# Revit family: 54-3334-001 DN350-600
name_source: partatom
category: Pipe Accessories
units: mm (PartAtom-declared; Revit-internal decimal feet)

## family parameters
Always vertical = No
Cut with Voids When Loaded = No
Part Type = Valve - Breaks Into
Round Connector Dimension = Use Diameter
Shared = No
Work Plane-Based = No

## types (25) — shared parameters
1 = 1 mm  [stored 0.00328084 ft]
50 = 40 mm
54-0350-33-0101100 = DN350_ PN10_ CTC
54-0350-33-1101100 = DN350_ PN16_ CTC
54-0350-34-0101100 = DN350_ PN10_ CTO
54-0350-34-1101100 = DN350_ PN16_ CTO
54-0400-33-0101100 = DN400_ PN10_ CTC
54-0400-33-1101100 = DN400_ PN16_ CTC
54-0400-33-1102100 = DN400_ PN16_ CTC
54-0400-34-0101100 = DN400_ PN10_ CTO
54-0400-34-1101100 = DN400_PN16_ CTO
54-0450-33-0101100 = DN450_ PN10_ CTC
54-0450-33-1101100 = DN450_ PN16_ CTC
54-0450-33-1102100 = DN450_ PN16_ CTC
54-0450-34-0101100 = DN450_ PN10_ CTO
54-0450-34-1101100 = DN450_ PN16_ CTO
54-0500-33-0101100 = DN500_ PN10_ CTC
54-0500-33-0102100 = DN500_ PN10_ CTC
54-0500-33-1101100 = DN500_ PN16_ CTC
54-0500-33-1102100 = DN500_ PN16_ CTC
54-0500-34-0101100 = DN500_ PN10_ CTO
54-0500-34-1101100 = DN500_ PN16_ CTO
54-0600-33-0101100 = DN600_ PN10_ CTC
54-0600-33-1101100 = DN600_ PN16_ CTC
54-0600-33-1102100 = DN600_ PN16_ CTC
54-0600-34-0101100 = DN600_ PN10_ CTO
54-0600-34-1101100 = DN600_ PN16_ CTO
Description_ = AVK GATE VALVE, FLANGED, METAL SEATED, PN10/16
F = 40 mm
F1 = 48 mm
F2 = 162 mm
H = 782 mm
Search_table = 54-3334-001 DN350-600
Stem_dim = 81 mm
URL product pages = https://www.avkvalves.com
stem_dim = 67.2 mm
sweep = 4 mm  [stored 0.0131234 ft]
zero-valued in all types: Default Elevation

## per-type parameters (varying)
- 54-0350-33-0101100: ACtuator_T=17.64 mm  [stored 0.057874 ft]; ADN=350 mm; Actuator_FLR=87.5 mm; BP_centre=50.5 mm; Body_H=391 mm; Body_L=448 mm; Body_T=167.5 mm; Body_W=198 mm; Body_rib_T=9.8 mm  [stored 0.0321522 ft]; Bonnet_FL_L=560 mm; Bonnet_FL_T=46.55 mm; Bonnet_FL_W=264 mm; Bonnet_dim1=89.6 mm; Bonnet_dim2=69.3 mm; Bonnet_dim3=649.06 mm; Bonnet_fillet=22 mm  [stored 0.0721785 ft]; Bore=175 mm; By_Vale_StemH1=168.75 mm; By_Vale_StemH2=177.19 mm; By_Vale_StemR1=14.67 mm; By_Vale_StemR2=26.4 mm; Bypass_DN=50 mm; Bypass_dim1=101 mm; Bypass_dim2=10.1 mm  [stored 0.0331365 ft]; Bypass_dim3=43.43 mm; Bypass_dis=430.95 mm; Bypass_dis/2=215.48 mm; Bypass_valve_H1=90 mm; Bypass_valve_H2=60 mm; Bypass_valve_H3=225 mm; Bypass_valve_W1=476.58 mm; Bypass_valve_W2=66 mm; Cut_dis=23.28 mm; DN=350 mm; FL_T=24.5 mm  [stored 0.0803806 ft]; Fillet=66 mm; H1=782 mm; H2=265 mm; L=381 mm; OD=505 mm; PN=10 mm  [stored 0.0328084 ft]; Raised_dia=429 mm; Raised_dis=4 mm  [stored 0.0131234 ft]; Rib_H=312.8 mm; Rib_L=252 mm; Rib_W=118.8 mm; W=787 mm; W-W1=280 mm; W1=507 mm; W1/2=253.5 mm; W_half=280 mm; bottom_rib=252.5 mm; bypass_sweep_dis=405.6 mm; wedge_dim1=217.8 mm
- 54-0350-33-1101100: ACtuator_T=19.08 mm  [stored 0.0625984 ft]; ADN=350 mm; Actuator_FLR=87.5 mm; BP_centre=53 mm; Body_H=391 mm; Body_L=448 mm; Body_T=167.5 mm; Body_W=198 mm; Body_rib_T=10.6 mm  [stored 0.0347769 ft]; Bonnet_FL_L=560 mm; Bonnet_FL_T=50.35 mm; Bonnet_FL_W=264 mm; Bonnet_dim1=89.6 mm; Bonnet_dim2=69.3 mm; Bonnet_dim3=649.06 mm; Bonnet_fillet=22 mm  [stored 0.0721785 ft]; Bore=175.05 mm; By_Vale_StemH1=168.75 mm; By_Vale_StemH2=177.19 mm; By_Vale_StemR1=14.67 mm; By_Vale_StemR2=26.4 mm; Bypass_DN=50 mm; Bypass_dim1=106 mm; Bypass_dim2=10.6 mm  [stored 0.0347769 ft]; Bypass_dim3=45.58 mm; Bypass_dis=430.95 mm; Bypass_dis/2=215.48 mm; Bypass_valve_H1=90 mm; Bypass_valve_H2=60 mm; Bypass_valve_H3=225 mm; Bypass_valve_W1=476.58 mm; Bypass_valve_W2=66 mm; Cut_dis=25.18 mm; DN=350.1 mm; FL_T=26.5 mm; Fillet=66 mm; H1=782 mm; H2=265 mm; L=381 mm; OD=530 mm; PN=16 mm  [stored 0.0524934 ft]; Raised_dia=429 mm; Raised_dis=4 mm  [stored 0.0131234 ft]; Rib_H=312.8 mm; Rib_L=252 mm; Rib_W=118.8 mm; W=787 mm; W-W1=280 mm; W1=507 mm; W1/2=253.5 mm; W_half=280 mm; bottom_rib=265 mm; bypass_sweep_dis=405.6 mm; wedge_dim1=217.8 mm
- 54-0350-34-0101100: ACtuator_T=17.64 mm  [stored 0.057874 ft]; ADN=350 mm; Actuator_FLR=87.5 mm; BP_centre=50.5 mm; Body_H=391 mm; Body_L=448 mm; Body_T=167.5 mm; Body_W=198 mm; Body_rib_T=9.8 mm  [stored 0.0321522 ft]; Bonnet_FL_L=560 mm; Bonnet_FL_T=46.55 mm; Bonnet_FL_W=264 mm; Bonnet_dim1=89.6 mm; Bonnet_dim2=69.3 mm; Bonnet_dim3=649.06 mm; Bonnet_fillet=22 mm  [stored 0.0721785 ft]; Bore=175.06 mm; By_Vale_StemH1=168.75 mm; By_Vale_StemH2=177.19 mm; By_Vale_StemR1=14.67 mm; By_Vale_StemR2=26.4 mm; Bypass_DN=50 mm; Bypass_dim1=101 mm; Bypass_dim2=10.1 mm  [stored 0.0331365 ft]; Bypass_dim3=43.43 mm; Bypass_dis=430.95 mm; Bypass_dis/2=215.48 mm; Bypass_valve_H1=90 mm; Bypass_valve_H2=60 mm; Bypass_valve_H3=225 mm; Bypass_valve_W1=476.58 mm; Bypass_valve_W2=66 mm; Cut_dis=23.28 mm; DN=350.11 mm; FL_T=24.5 mm  [stored 0.0803806 ft]; Fillet=66 mm; H1=782 mm; H2=265 mm; L=381 mm; OD=505 mm; PN=10 mm  [stored 0.0328084 ft]; Raised_dia=429 mm; Raised_dis=4 mm  [stored 0.0131234 ft]; Rib_H=312.8 mm; Rib_L=252 mm; Rib_W=118.8 mm; W=787 mm; W-W1=280 mm; W1=507 mm; W1/2=253.5 mm; W_half=280 mm; bottom_rib=252.5 mm; bypass_sweep_dis=405.6 mm; wedge_dim1=217.8 mm
- 54-0350-34-1101100: ACtuator_T=19.08 mm  [stored 0.0625984 ft]; ADN=350 mm; Actuator_FLR=87.5 mm; BP_centre=53 mm; Body_H=391 mm; Body_L=448 mm; Body_T=167.5 mm; Body_W=198 mm; Body_rib_T=10.6 mm  [stored 0.0347769 ft]; Bonnet_FL_L=560 mm; Bonnet_FL_T=50.35 mm; Bonnet_FL_W=264 mm; Bonnet_dim1=89.6 mm; Bonnet_dim2=69.3 mm; Bonnet_dim3=649.06 mm; Bonnet_fillet=22 mm  [stored 0.0721785 ft]; Bore=175.06 mm; By_Vale_StemH1=168.75 mm; By_Vale_StemH2=177.19 mm; By_Vale_StemR1=14.67 mm; By_Vale_StemR2=26.4 mm; Bypass_DN=50 mm; Bypass_dim1=106 mm; Bypass_dim2=10.6 mm  [stored 0.0347769 ft]; Bypass_dim3=45.58 mm; Bypass_dis=430.95 mm; Bypass_dis/2=215.48 mm; Bypass_valve_H1=90 mm; Bypass_valve_H2=60 mm; Bypass_valve_H3=225 mm; Bypass_valve_W1=476.58 mm; Bypass_valve_W2=66 mm; Cut_dis=25.18 mm; DN=350.12 mm; FL_T=26.5 mm; Fillet=66 mm; H1=782 mm; H2=265 mm; L=381 mm; OD=530 mm; PN=16 mm  [stored 0.0524934 ft]; Raised_dia=429 mm; Raised_dis=4 mm  [stored 0.0131234 ft]; Rib_H=312.8 mm; Rib_L=252 mm; Rib_W=118.8 mm; W=787 mm; W-W1=280 mm; W1=507 mm; W1/2=253.5 mm; W_half=280 mm; bottom_rib=265 mm; bypass_sweep_dis=405.6 mm; wedge_dim1=217.8 mm
- 54-0400-33-0101100: ACtuator_T=17.64 mm  [stored 0.057874 ft]; ADN=400 mm; Actuator_FLR=87.5 mm; BP_centre=56.5 mm; Body_H=428.5 mm; Body_L=483.2 mm; Body_T=192.5 mm; Body_W=198 mm; Body_rib_T=9.8 mm  [stored 0.0321522 ft]; Bonnet_FL_L=604 mm; Bonnet_FL_T=46.55 mm; Bonnet_FL_W=264 mm; Bonnet_dim1=96.64 mm; Bonnet_dim2=69.3 mm; Bonnet_dim3=711.31 mm; Bonnet_fillet=22 mm  [stored 0.0721785 ft]; Bore=200 mm; By_Vale_StemH1=168.75 mm; By_Vale_StemH2=177.19 mm; By_Vale_StemR1=14.67 mm; By_Vale_StemR2=26.4 mm; Bypass_DN=50 mm; Bypass_dim1=113 mm; Bypass_dim2=11.3 mm  [stored 0.0370735 ft]; Bypass_dim3=48.59 mm; Bypass_dis=456.45 mm; Bypass_dis/2=228.23 mm; Bypass_valve_H1=90 mm; Bypass_valve_H2=60 mm; Bypass_valve_H3=225 mm; Bypass_valve_W1=504.78 mm; Bypass_valve_W2=66 mm; Cut_dis=23.28 mm; DN=400 mm; FL_T=24.5 mm  [stored 0.0803806 ft]; Fillet=66 mm; H1=857 mm; H2=295 mm; L=406 mm; OD=565 mm; PN=10 mm  [stored 0.0328084 ft]; Raised_dia=480 mm; Raised_dis=4 mm  [stored 0.0131234 ft]; Rib_H=342.8 mm; Rib_L=271.8 mm; Rib_W=118.8 mm; W=839 mm; W-W1=302 mm; W1=537 mm; W1/2=268.5 mm; W_half=302 mm; bottom_rib=282.5 mm; bypass_sweep_dis=429.6 mm; wedge_dim1=217.8 mm
- 54-0400-33-1101100: ACtuator_T=20.16 mm  [stored 0.0661417 ft]; ADN=400 mm; Actuator_FLR=87.5 mm; BP_centre=59 mm; Body_H=428.5 mm; Body_L=483.2 mm; Body_T=192.5 mm; Body_W=198 mm; Body_rib_T=11.2 mm  [stored 0.0367454 ft]; Bonnet_FL_L=604 mm; Bonnet_FL_T=53.2 mm; Bonnet_FL_W=264 mm; Bonnet_dim1=96.64 mm; Bonnet_dim2=69.3 mm; Bonnet_dim3=711.31 mm; Bonnet_fillet=22 mm  [stored 0.0721785 ft]; Bore=200.05 mm; By_Vale_StemH1=168.75 mm; By_Vale_StemH2=177.19 mm; By_Vale_StemR1=14.67 mm; By_Vale_StemR2=26.4 mm; Bypass_DN=50 mm; Bypass_dim1=118 mm; Bypass_dim2=11.8 mm  [stored 0.0387139 ft]; Bypass_dim3=50.74 mm; Bypass_dis=456.45 mm; Bypass_dis/2=228.23 mm; Bypass_valve_H1=90 mm; Bypass_valve_H2=60 mm; Bypass_valve_H3=225 mm; Bypass_valve_W1=504.78 mm; Bypass_valve_W2=66 mm; Cut_dis=26.6 mm; DN=400.1 mm; FL_T=28 mm; Fillet=66 mm; H1=857 mm; H2=295 mm; L=406 mm; OD=590 mm; PN=16 mm  [stored 0.0524934 ft]; Raised_dia=480 mm; Raised_dis=4 mm  [stored 0.0131234 ft]; Rib_H=342.8 mm; Rib_L=271.8 mm; Rib_W=118.8 mm; W=839 mm; W-W1=302 mm; W1=537 mm; W1/2=268.5 mm; W_half=302 mm; bottom_rib=295 mm; bypass_sweep_dis=429.6 mm; wedge_dim1=217.8 mm
- 54-0400-33-1102100: ACtuator_T=20.16 mm  [stored 0.0661417 ft]; ADN=400 mm; Actuator_FLR=105 mm; BP_centre=59 mm; Body_H=428.5 mm; Body_L=483.2 mm; Body_T=192.5 mm; Body_W=198 mm; Body_rib_T=11.2 mm  [stored 0.0367454 ft]; Bonnet_FL_L=604 mm; Bonnet_FL_T=53.2 mm; Bonnet_FL_W=264 mm; Bonnet_dim1=96.64 mm; Bonnet_dim2=69.3 mm; Bonnet_dim3=711.31 mm; Bonnet_fillet=22 mm  [stored 0.0721785 ft]; Bore=200.06 mm; By_Vale_StemH1=168.75 mm; By_Vale_StemH2=177.19 mm; By_Vale_StemR1=14.67 mm; By_Vale_StemR2=26.4 mm; Bypass_DN=50 mm; Bypass_dim1=118 mm; Bypass_dim2=11.8 mm  [stored 0.0387139 ft]; Bypass_dim3=50.74 mm; Bypass_dis=456.45 mm; Bypass_dis/2=228.23 mm; Bypass_valve_H1=90 mm; Bypass_valve_H2=60 mm; Bypass_valve_H3=225 mm; Bypass_valve_W1=504.78 mm; Bypass_valve_W2=66 mm; Cut_dis=26.6 mm; DN=400.11 mm; FL_T=28 mm; Fillet=66 mm; H1=857 mm; H2=295 mm; L=406 mm; OD=590 mm; PN=16 mm  [stored 0.0524934 ft]; Raised_dia=480 mm; Raised_dis=4 mm  [stored 0.0131234 ft]; Rib_H=342.8 mm; Rib_L=271.8 mm; Rib_W=118.8 mm; W=839 mm; W-W1=302 mm; W1=537 mm; W1/2=268.5 mm; W_half=302 mm; bottom_rib=295 mm; bypass_sweep_dis=429.6 mm; wedge_dim1=217.8 mm
- 54-0400-34-0101100: ACtuator_T=17.64 mm  [stored 0.057874 ft]; ADN=400 mm; Actuator_FLR=87.5 mm; BP_centre=56.5 mm; Body_H=428.5 mm; Body_L=483.2 mm; Body_T=192.5 mm; Body_W=198 mm; Body_rib_T=9.8 mm  [stored 0.0321522 ft]; Bonnet_FL_L=604 mm; Bonnet_FL_T=46.55 mm; Bonnet_FL_W=264 mm; Bonnet_dim1=96.64 mm; Bonnet_dim2=69.3 mm; Bonnet_dim3=711.31 mm; Bonnet_fillet=22 mm  [stored 0.0721785 ft]; Bore=200.06 mm; By_Vale_StemH1=168.75 mm; By_Vale_StemH2=177.19 mm; By_Vale_StemR1=14.67 mm; By_Vale_StemR2=26.4 mm; Bypass_DN=50 mm; Bypass_dim1=113 mm; Bypass_dim2=11.3 mm  [stored 0.0370735 ft]; Bypass_dim3=48.59 mm; Bypass_dis=456.45 mm; Bypass_dis/2=228.23 mm; Bypass_valve_H1=90 mm; Bypass_valve_H2=60 mm; Bypass_valve_H3=225 mm; Bypass_valve_W1=504.78 mm; Bypass_valve_W2=66 mm; Cut_dis=23.28 mm; DN=400.12 mm; FL_T=24.5 mm  [stored 0.0803806 ft]; Fillet=66 mm; H1=857 mm; H2=295 mm; L=406 mm; OD=565 mm; PN=10 mm  [stored 0.0328084 ft]; Raised_dia=480 mm; Raised_dis=4 mm  [stored 0.0131234 ft]; Rib_H=342.8 mm; Rib_L=271.8 mm; Rib_W=118.8 mm; W=839 mm; W-W1=302 mm; W1=537 mm; W1/2=268.5 mm; W_half=302 mm; bottom_rib=282.5 mm; bypass_sweep_dis=429.6 mm; wedge_dim1=217.8 mm
- 54-0400-34-1101100: ACtuator_T=20.16 mm  [stored 0.0661417 ft]; ADN=400 mm; Actuator_FLR=87.5 mm; BP_centre=59 mm; Body_H=428.5 mm; Body_L=483.2 mm; Body_T=192.5 mm; Body_W=198 mm; Body_rib_T=11.2 mm  [stored 0.0367454 ft]; Bonnet_FL_L=604 mm; Bonnet_FL_T=53.2 mm; Bonnet_FL_W=264 mm; Bonnet_dim1=96.64 mm; Bonnet_dim2=69.3 mm; Bonnet_dim3=711.31 mm; Bonnet_fillet=22 mm  [stored 0.0721785 ft]; Bore=200.07 mm; By_Vale_StemH1=168.75 mm; By_Vale_StemH2=177.19 mm; By_Vale_StemR1=14.67 mm; By_Vale_StemR2=26.4 mm; Bypass_DN=50 mm; Bypass_dim1=118 mm; Bypass_dim2=11.8 mm  [stored 0.0387139 ft]; Bypass_dim3=50.74 mm; Bypass_dis=456.45 mm; Bypass_dis/2=228.23 mm; Bypass_valve_H1=90 mm; Bypass_valve_H2=60 mm; Bypass_valve_H3=225 mm; Bypass_valve_W1=504.78 mm; Bypass_valve_W2=66 mm; Cut_dis=26.6 mm; DN=400.13 mm; FL_T=28 mm; Fillet=66 mm; H1=857 mm; H2=295 mm; L=406 mm; OD=590 mm; PN=16 mm  [stored 0.0524934 ft]; Raised_dia=480 mm; Raised_dis=4 mm  [stored 0.0131234 ft]; Rib_H=342.8 mm; Rib_L=271.8 mm; Rib_W=118.8 mm; W=839 mm; W-W1=302 mm; W1=537 mm; W1/2=268.5 mm; W_half=302 mm; bottom_rib=295 mm; bypass_sweep_dis=429.6 mm; wedge_dim1=217.8 mm
- 54-0450-33-0101100: ACtuator_T=18.36 mm  [stored 0.0602362 ft]; ADN=450 mm; Actuator_FLR=87.5 mm; BP_centre=61.5 mm; Body_H=472 mm; Body_L=536 mm; Body_T=217.5 mm; Body_W=217.5 mm; Body_rib_T=10.2 mm  [stored 0.0334646 ft]; Bonnet_FL_L=670 mm; Bonnet_FL_T=48.45 mm; Bonnet_FL_W=290 mm; Bonnet_dim1=107.2 mm; Bonnet_dim2=76.13 mm; Bonnet_dim3=783.52 mm; Bonnet_fillet=24.17 mm; Bore=225 mm; By_Vale_StemH1=270 mm; By_Vale_StemH2=283.5 mm; By_Vale_StemR1=16.11 mm; By_Vale_StemR2=29 mm; Bypass_DN=80 mm; Bypass_dim1=123 mm; Bypass_dim2=12.3 mm; Bypass_dim3=52.89 mm; Bypass_dis=507.45 mm; Bypass_dis/2=253.73 mm; Bypass_valve_H1=144 mm; Bypass_valve_H2=96 mm; Bypass_valve_H3=360 mm; Bypass_valve_W1=561.18 mm; Bypass_valve_W2=72.5 mm; Cut_dis=24.23 mm; DN=450 mm; FL_T=25.5 mm  [stored 0.0836614 ft]; Fillet=72.5 mm; H1=944 mm; H2=325 mm; L=432 mm; OD=615 mm; PN=10 mm  [stored 0.0328084 ft]; Raised_dia=530 mm; Raised_dis=4 mm  [stored 0.0131234 ft]; Rib_H=377.6 mm; Rib_L=301.5 mm; Rib_W=130.5 mm; W=932 mm; W-W1=335 mm; W1=597 mm; W1/2=298.5 mm; W_half=335 mm; bottom_rib=307.5 mm; bypass_sweep_dis=477.6 mm; wedge_dim1=239.25 mm
- 54-0450-33-1101100: ACtuator_T=21.6 mm  [stored 0.0708661 ft]; ADN=450 mm; Actuator_FLR=87.5 mm; BP_centre=65 mm; Body_H=472 mm; Body_L=536 mm; Body_T=217.5 mm; Body_W=217.5 mm; Body_rib_T=12 mm  [stored 0.0393701 ft]; Bonnet_FL_L=670 mm; Bonnet_FL_T=57 mm; Bonnet_FL_W=290 mm; Bonnet_dim1=107.2 mm; Bonnet_dim2=76.13 mm; Bonnet_dim3=783.52 mm; Bonnet_fillet=24.17 mm; Bore=225.05 mm; By_Vale_StemH1=270 mm; By_Vale_StemH2=283.5 mm; By_Vale_StemR1=16.11 mm; By_Vale_StemR2=29 mm; Bypass_DN=80 mm; Bypass_dim1=130 mm; Bypass_dim2=13 mm  [stored 0.0426509 ft]; Bypass_dim3=55.9 mm; Bypass_dis=507.45 mm; Bypass_dis/2=253.73 mm; Bypass_valve_H1=144 mm; Bypass_valve_H2=96 mm; Bypass_valve_H3=360 mm; Bypass_valve_W1=561.18 mm; Bypass_valve_W2=72.5 mm; Cut_dis=28.5 mm; DN=450.1 mm; FL_T=30 mm; Fillet=72.5 mm; H1=944 mm; H2=325 mm; L=432 mm; OD=650 mm; PN=16 mm  [stored 0.0524934 ft]; Raised_dia=548 mm; Raised_dis=4 mm  [stored 0.0131234 ft]; Rib_H=377.6 mm; Rib_L=301.5 mm; Rib_W=130.5 mm; W=932 mm; W-W1=335 mm; W1=597 mm; W1/2=298.5 mm; W_half=335 mm; bottom_rib=325 mm; bypass_sweep_dis=477.6 mm; wedge_dim1=239.25 mm
- 54-0450-33-1102100: ACtuator_T=21.6 mm  [stored 0.0708661 ft]; ADN=450 mm; Actuator_FLR=105 mm; BP_centre=65 mm; Body_H=472 mm; Body_L=536 mm; Body_T=217.5 mm; Body_W=217.5 mm; Body_rib_T=12 mm  [stored 0.0393701 ft]; Bonnet_FL_L=670 mm; Bonnet_FL_T=57 mm; Bonnet_FL_W=290 mm; Bonnet_dim1=107.2 mm; Bonnet_dim2=76.13 mm; Bonnet_dim3=783.52 mm; Bonnet_fillet=24.17 mm; Bore=225.06 mm; By_Vale_StemH1=270 mm; By_Vale_StemH2=283.5 mm; By_Vale_StemR1=16.11 mm; By_Vale_StemR2=29 mm; Bypass_DN=80 mm; Bypass_dim1=130 mm; Bypass_dim2=13 mm  [stored 0.0426509 ft]; Bypass_dim3=55.9 mm; Bypass_dis=507.45 mm; Bypass_dis/2=253.73 mm; Bypass_valve_H1=144 mm; Bypass_valve_H2=96 mm; Bypass_valve_H3=360 mm; Bypass_valve_W1=561.18 mm; Bypass_valve_W2=72.5 mm; Cut_dis=28.5 mm; DN=450.11 mm; FL_T=30 mm; Fillet=72.5 mm; H1=944 mm; H2=325 mm; L=432 mm; OD=650 mm; PN=16 mm  [stored 0.0524934 ft]; Raised_dia=548 mm; Raised_dis=4 mm  [stored 0.0131234 ft]; Rib_H=377.6 mm; Rib_L=301.5 mm; Rib_W=130.5 mm; W=932 mm; W-W1=335 mm; W1=597 mm; W1/2=298.5 mm; W_half=335 mm; bottom_rib=325 mm; bypass_sweep_dis=477.6 mm; wedge_dim1=239.25 mm
- 54-0450-34-0101100: ACtuator_T=18.36 mm  [stored 0.0602362 ft]; ADN=450 mm; Actuator_FLR=87.5 mm; BP_centre=61.5 mm; Body_H=472 mm; Body_L=536 mm; Body_T=217.5 mm; Body_W=217.5 mm; Body_rib_T=10.2 mm  [stored 0.0334646 ft]; Bonnet_FL_L=670 mm; Bonnet_FL_T=48.45 mm; Bonnet_FL_W=290 mm; Bonnet_dim1=107.2 mm; Bonnet_dim2=76.13 mm; Bonnet_dim3=783.52 mm; Bonnet_fillet=24.17 mm; Bore=225.06 mm; By_Vale_StemH1=270 mm; By_Vale_StemH2=283.5 mm; By_Vale_StemR1=16.11 mm; By_Vale_StemR2=29 mm; Bypass_DN=80 mm; Bypass_dim1=123 mm; Bypass_dim2=12.3 mm; Bypass_dim3=52.89 mm; Bypass_dis=507.45 mm; Bypass_dis/2=253.73 mm; Bypass_valve_H1=144 mm; Bypass_valve_H2=96 mm; Bypass_valve_H3=360 mm; Bypass_valve_W1=561.18 mm; Bypass_valve_W2=72.5 mm; Cut_dis=24.23 mm; DN=450.12 mm; FL_T=25.5 mm  [stored 0.0836614 ft]; Fillet=72.5 mm; H1=944 mm; H2=325 mm; L=432 mm; OD=615 mm; PN=10 mm  [stored 0.0328084 ft]; Raised_dia=530 mm; Raised_dis=4 mm  [stored 0.0131234 ft]; Rib_H=377.6 mm; Rib_L=301.5 mm; Rib_W=130.5 mm; W=932 mm; W-W1=335 mm; W1=597 mm; W1/2=298.5 mm; W_half=335 mm; bottom_rib=307.5 mm; bypass_sweep_dis=477.6 mm; wedge_dim1=239.25 mm
- 54-0450-34-1101100: ACtuator_T=21.6 mm  [stored 0.0708661 ft]; ADN=450 mm; Actuator_FLR=87.5 mm; BP_centre=65 mm; Body_H=472 mm; Body_L=536 mm; Body_T=217.5 mm; Body_W=217.5 mm; Body_rib_T=12 mm  [stored 0.0393701 ft]; Bonnet_FL_L=670 mm; Bonnet_FL_T=57 mm; Bonnet_FL_W=290 mm; Bonnet_dim1=107.2 mm; Bonnet_dim2=76.13 mm; Bonnet_dim3=783.52 mm; Bonnet_fillet=24.17 mm; Bore=225.07 mm; By_Vale_StemH1=270 mm; By_Vale_StemH2=283.5 mm; By_Vale_StemR1=16.11 mm; By_Vale_StemR2=29 mm; Bypass_DN=80 mm; Bypass_dim1=130 mm; Bypass_dim2=13 mm  [stored 0.0426509 ft]; Bypass_dim3=55.9 mm; Bypass_dis=507.45 mm; Bypass_dis/2=253.73 mm; Bypass_valve_H1=144 mm; Bypass_valve_H2=96 mm; Bypass_valve_H3=360 mm; Bypass_valve_W1=561.18 mm; Bypass_valve_W2=72.5 mm; Cut_dis=28.5 mm; DN=450.13 mm; FL_T=30 mm; Fillet=72.5 mm; H1=944 mm; H2=325 mm; L=432 mm; OD=650 mm; PN=16 mm  [stored 0.0524934 ft]; Raised_dia=548 mm; Raised_dis=4 mm  [stored 0.0131234 ft]; Rib_H=377.6 mm; Rib_L=301.5 mm; Rib_W=130.5 mm; W=932 mm; W-W1=335 mm; W1=597 mm; W1/2=298.5 mm; W_half=335 mm; bottom_rib=325 mm; bypass_sweep_dis=477.6 mm; wedge_dim1=239.25 mm
- 54-0500-33-0101100: ACtuator_T=19.08 mm  [stored 0.0625984 ft]; ADN=450 mm; Actuator_FLR=87.5 mm; BP_centre=67 mm; Body_H=508.5 mm; Body_L=536 mm; Body_T=217.5 mm; Body_W=217.5 mm; Body_rib_T=10.6 mm  [stored 0.0347769 ft]; Bonnet_FL_L=670 mm; Bonnet_FL_T=50.35 mm; Bonnet_FL_W=290 mm; Bonnet_dim1=107.2 mm; Bonnet_dim2=76.13 mm; Bonnet_dim3=844.11 mm; Bonnet_fillet=24.17 mm; Bore=250 mm; By_Vale_StemH1=270 mm; By_Vale_StemH2=283.5 mm; By_Vale_StemR1=16.11 mm; By_Vale_StemR2=29 mm; Bypass_DN=80 mm; Bypass_dim1=134 mm; Bypass_dim2=13.4 mm  [stored 0.0439633 ft]; Bypass_dim3=57.62 mm; Bypass_dis=541.45 mm; Bypass_dis/2=270.73 mm; Bypass_valve_H1=144 mm; Bypass_valve_H2=96 mm; Bypass_valve_H3=360 mm; Bypass_valve_W1=598.78 mm; Bypass_valve_W2=72.5 mm; Cut_dis=25.18 mm; DN=500 mm; FL_T=26.5 mm; Fillet=72.5 mm; H1=1017 mm; H2=365 mm; L=457 mm; OD=670 mm; PN=10 mm  [stored 0.0328084 ft]; Raised_dia=582 mm; Raised_dis=4 mm  [stored 0.0131234 ft]; Rib_H=406.8 mm; Rib_L=301.5 mm; Rib_W=130.5 mm; W=1002 mm; W-W1=365 mm; W1=637 mm; W1/2=318.5 mm; W_half=365 mm; bottom_rib=335 mm; bypass_sweep_dis=509.6 mm; wedge_dim1=239.25 mm
- 54-0500-33-0102100: ACtuator_T=19.08 mm  [stored 0.0625984 ft]; ADN=450 mm; Actuator_FLR=105 mm; BP_centre=67 mm; Body_H=508.5 mm; Body_L=536 mm; Body_T=217.5 mm; Body_W=217.5 mm; Body_rib_T=10.6 mm  [stored 0.0347769 ft]; Bonnet_FL_L=670 mm; Bonnet_FL_T=50.35 mm; Bonnet_FL_W=290 mm; Bonnet_dim1=107.2 mm; Bonnet_dim2=76.13 mm; Bonnet_dim3=844.11 mm; Bonnet_fillet=24.17 mm; Bore=250.05 mm; By_Vale_StemH1=270 mm; By_Vale_StemH2=283.5 mm; By_Vale_StemR1=16.11 mm; By_Vale_StemR2=29 mm; Bypass_DN=80 mm; Bypass_dim1=134 mm; Bypass_dim2=13.4 mm  [stored 0.0439633 ft]; Bypass_dim3=57.62 mm; Bypass_dis=541.45 mm; Bypass_dis/2=270.73 mm; Bypass_valve_H1=144 mm; Bypass_valve_H2=96 mm; Bypass_valve_H3=360 mm; Bypass_valve_W1=598.78 mm; Bypass_valve_W2=72.5 mm; Cut_dis=25.18 mm; DN=500.1 mm; FL_T=26.5 mm; Fillet=72.5 mm; H1=1017 mm; H2=365 mm; L=457 mm; OD=670 mm; PN=10 mm  [stored 0.0328084 ft]; Raised_dia=582 mm; Raised_dis=4 mm  [stored 0.0131234 ft]; Rib_H=406.8 mm; Rib_L=301.5 mm; Rib_W=130.5 mm; W=1002 mm; W-W1=365 mm; W1=637 mm; W1/2=318.5 mm; W_half=365 mm; bottom_rib=335 mm; bypass_sweep_dis=509.6 mm; wedge_dim1=239.25 mm
- 54-0500-33-1101100: ACtuator_T=22.68 mm  [stored 0.0744094 ft]; ADN=500 mm; Actuator_FLR=87.5 mm; BP_centre=73 mm; Body_H=508.5 mm; Body_L=584 mm; Body_T=242.5 mm; Body_W=225 mm; Body_rib_T=12.6 mm  [stored 0.0413386 ft]; Bonnet_FL_L=730 mm; Bonnet_FL_T=59.85 mm; Bonnet_FL_W=300 mm; Bonnet_dim1=116.8 mm; Bonnet_dim2=78.75 mm; Bonnet_dim3=844.11 mm; Bonnet_fillet=25 mm  [stored 0.082021 ft]; Bore=250.06 mm; By_Vale_StemH1=270 mm; By_Vale_StemH2=283.5 mm; By_Vale_StemR1=16.67 mm; By_Vale_StemR2=30 mm; Bypass_DN=80 mm; Bypass_dim1=146 mm; Bypass_dim2=14.6 mm  [stored 0.0479003 ft]; Bypass_dim3=62.78 mm; Bypass_dis=541.45 mm; Bypass_dis/2=270.73 mm; Bypass_valve_H1=144 mm; Bypass_valve_H2=96 mm; Bypass_valve_H3=360 mm; Bypass_valve_W1=598.78 mm; Bypass_valve_W2=75 mm; Cut_dis=29.93 mm; DN=500.11 mm; FL_T=31.5 mm; Fillet=75 mm; H1=1017 mm; H2=365 mm; L=457 mm; OD=730 mm; PN=16 mm  [stored 0.0524934 ft]; Raised_dia=609 mm; Raised_dis=4 mm  [stored 0.0131234 ft]; Rib_H=406.8 mm; Rib_L=328.5 mm; Rib_W=135 mm; W=1002 mm; W-W1=365 mm; W1=637 mm; W1/2=318.5 mm; W_half=365 mm; bottom_rib=365 mm; bypass_sweep_dis=509.6 mm; wedge_dim1=247.5 mm
- 54-0500-33-1102100: ACtuator_T=22.68 mm  [stored 0.0744094 ft]; ADN=500 mm; Actuator_FLR=105 mm; BP_centre=73 mm; Body_H=508.5 mm; Body_L=584 mm; Body_T=242.5 mm; Body_W=225 mm; Body_rib_T=12.6 mm  [stored 0.0413386 ft]; Bonnet_FL_L=730 mm; Bonnet_FL_T=59.85 mm; Bonnet_FL_W=300 mm; Bonnet_dim1=116.8 mm; Bonnet_dim2=78.75 mm; Bonnet_dim3=844.11 mm; Bonnet_fillet=25 mm  [stored 0.082021 ft]; Bore=250.06 mm; By_Vale_StemH1=270 mm; By_Vale_StemH2=283.5 mm; By_Vale_StemR1=16.67 mm; By_Vale_StemR2=30 mm; Bypass_DN=80 mm; Bypass_dim1=146 mm; Bypass_dim2=14.6 mm  [stored 0.0479003 ft]; Bypass_dim3=62.78 mm; Bypass_dis=541.45 mm; Bypass_dis/2=270.73 mm; Bypass_valve_H1=144 mm; Bypass_valve_H2=96 mm; Bypass_valve_H3=360 mm; Bypass_valve_W1=598.78 mm; Bypass_valve_W2=75 mm; Cut_dis=29.93 mm; DN=500.12 mm; FL_T=31.5 mm; Fillet=75 mm; H1=1017 mm; H2=365 mm; L=457 mm; OD=730 mm; PN=16 mm  [stored 0.0524934 ft]; Raised_dia=609 mm; Raised_dis=4 mm  [stored 0.0131234 ft]; Rib_H=406.8 mm; Rib_L=328.5 mm; Rib_W=135 mm; W=1002 mm; W-W1=365 mm; W1=637 mm; W1/2=318.5 mm; W_half=365 mm; bottom_rib=365 mm; bypass_sweep_dis=509.6 mm; wedge_dim1=247.5 mm
- 54-0500-34-0101100: ACtuator_T=19.08 mm  [stored 0.0625984 ft]; ADN=500 mm; Actuator_FLR=87.5 mm; BP_centre=67 mm; Body_H=508.5 mm; Body_L=584 mm; Body_T=242.5 mm; Body_W=225 mm; Body_rib_T=10.6 mm  [stored 0.0347769 ft]; Bonnet_FL_L=730 mm; Bonnet_FL_T=50.35 mm; Bonnet_FL_W=300 mm; Bonnet_dim1=116.8 mm; Bonnet_dim2=78.75 mm; Bonnet_dim3=844.11 mm; Bonnet_fillet=25 mm  [stored 0.082021 ft]; Bore=250.07 mm; By_Vale_StemH1=270 mm; By_Vale_StemH2=283.5 mm; By_Vale_StemR1=16.67 mm; By_Vale_StemR2=30 mm; Bypass_DN=80 mm; Bypass_dim1=134 mm; Bypass_dim2=13.4 mm  [stored 0.0439633 ft]; Bypass_dim3=57.62 mm; Bypass_dis=541.45 mm; Bypass_dis/2=270.73 mm; Bypass_valve_H1=144 mm; Bypass_valve_H2=96 mm; Bypass_valve_H3=360 mm; Bypass_valve_W1=598.78 mm; Bypass_valve_W2=75 mm; Cut_dis=25.18 mm; DN=500.13 mm; FL_T=26.5 mm; Fillet=75 mm; H1=1017 mm; H2=365 mm; L=457 mm; OD=670 mm; PN=10 mm  [stored 0.0328084 ft]; Raised_dia=582 mm; Raised_dis=4 mm  [stored 0.0131234 ft]; Rib_H=406.8 mm; Rib_L=328.5 mm; Rib_W=135 mm; W=1002 mm; W-W1=365 mm; W1=637 mm; W1/2=318.5 mm; W_half=365 mm; bottom_rib=335 mm; bypass_sweep_dis=509.6 mm; wedge_dim1=247.5 mm
- 54-0500-34-1101100: ACtuator_T=22.68 mm  [stored 0.0744094 ft]; ADN=500 mm; Actuator_FLR=87.5 mm; BP_centre=73 mm; Body_H=508.5 mm; Body_L=584 mm; Body_T=242.5 mm; Body_W=225 mm; Body_rib_T=12.6 mm  [stored 0.0413386 ft]; Bonnet_FL_L=730 mm; Bonnet_FL_T=59.85 mm; Bonnet_FL_W=300 mm; Bonnet_dim1=116.8 mm; Bonnet_dim2=78.75 mm; Bonnet_dim3=844.11 mm; Bonnet_fillet=25 mm  [stored 0.082021 ft]; Bore=250.07 mm; By_Vale_StemH1=270 mm; By_Vale_StemH2=283.5 mm; By_Vale_StemR1=16.67 mm; By_Vale_StemR2=30 mm; Bypass_DN=80 mm; Bypass_dim1=146 mm; Bypass_dim2=14.6 mm  [stored 0.0479003 ft]; Bypass_dim3=62.78 mm; Bypass_dis=541.45 mm; Bypass_dis/2=270.73 mm; Bypass_valve_H1=144 mm; Bypass_valve_H2=96 mm; Bypass_valve_H3=360 mm; Bypass_valve_W1=598.78 mm; Bypass_valve_W2=75 mm; Cut_dis=29.93 mm; DN=500.14 mm; FL_T=31.5 mm; Fillet=75 mm; H1=1017 mm; H2=365 mm; L=457 mm; OD=730 mm; PN=16 mm  [stored 0.0524934 ft]; Raised_dia=609 mm; Raised_dis=4 mm  [stored 0.0131234 ft]; Rib_H=406.8 mm; Rib_L=328.5 mm; Rib_W=135 mm; W=1002 mm; W-W1=365 mm; W1=637 mm; W1/2=318.5 mm; W_half=365 mm; bottom_rib=365 mm; bypass_sweep_dis=509.6 mm; wedge_dim1=247.5 mm
- 54-0600-33-0101100: ACtuator_T=21.6 mm  [stored 0.0708661 ft]; ADN=500 mm; Actuator_FLR=87.5 mm; BP_centre=78 mm; Body_H=589 mm; Body_L=584 mm; Body_T=242.5 mm; Body_W=225 mm; Body_rib_T=12 mm  [stored 0.0393701 ft]; Bonnet_FL_L=730 mm; Bonnet_FL_T=57 mm; Bonnet_FL_W=300 mm; Bonnet_dim1=116.8 mm; Bonnet_dim2=78.75 mm; Bonnet_dim3=977.74 mm; Bonnet_fillet=25 mm  [stored 0.082021 ft]; Bore=300 mm; By_Vale_StemH1=270 mm; By_Vale_StemH2=283.5 mm; By_Vale_StemR1=16.67 mm; By_Vale_StemR2=30 mm; Bypass_DN=80 mm; Bypass_dim1=156 mm; Bypass_dim2=15.6 mm  [stored 0.0511811 ft]; Bypass_dim3=67.08 mm; Bypass_dis=592.45 mm; Bypass_dis/2=296.23 mm; Bypass_valve_H1=144 mm; Bypass_valve_H2=96 mm; Bypass_valve_H3=360 mm; Bypass_valve_W1=655.18 mm; Bypass_valve_W2=75 mm; Cut_dis=28.5 mm; DN=600 mm; FL_T=30 mm; Fillet=75 mm; H1=1178 mm; H2=440 mm; L=508 mm; OD=780 mm; PN=10 mm  [stored 0.0328084 ft]; Raised_dia=682 mm; Raised_dis=4 mm  [stored 0.0131234 ft]; Rib_H=471.2 mm; Rib_L=328.5 mm; Rib_W=135 mm; W=1117 mm; W-W1=420 mm; W1=697 mm; W1/2=348.5 mm; W_half=420 mm; bottom_rib=390 mm; bypass_sweep_dis=557.6 mm; wedge_dim1=247.5 mm
- 54-0600-33-1101100: ACtuator_T=25.92 mm; ADN=500 mm; Actuator_FLR=87.5 mm; BP_centre=73 mm; Body_H=589 mm; Body_L=584 mm; Body_T=242.5 mm; Body_W=225 mm; Body_rib_T=14.4 mm  [stored 0.0472441 ft]; Bonnet_FL_L=730 mm; Bonnet_FL_T=68.4 mm; Bonnet_FL_W=300 mm; Bonnet_dim1=116.8 mm; Bonnet_dim2=78.75 mm; Bonnet_dim3=977.74 mm; Bonnet_fillet=25 mm  [stored 0.082021 ft]; Bore=300.05 mm; By_Vale_StemH1=270 mm; By_Vale_StemH2=283.5 mm; By_Vale_StemR1=16.67 mm; By_Vale_StemR2=30 mm; Bypass_DN=80 mm; Bypass_dim1=146 mm; Bypass_dim2=14.6 mm  [stored 0.0479003 ft]; Bypass_dim3=62.78 mm; Bypass_dis=592.45 mm; Bypass_dis/2=296.23 mm; Bypass_valve_H1=144 mm; Bypass_valve_H2=96 mm; Bypass_valve_H3=360 mm; Bypass_valve_W1=655.18 mm; Bypass_valve_W2=75 mm; Cut_dis=34.2 mm; DN=600.1 mm; FL_T=36 mm; Fillet=75 mm; H1=1178 mm; H2=440 mm; L=508 mm; OD=730 mm; PN=16 mm  [stored 0.0524934 ft]; Raised_dia=609 mm; Raised_dis=4 mm  [stored 0.0131234 ft]; Rib_H=471.2 mm; Rib_L=328.5 mm; Rib_W=135 mm; W=1117 mm; W-W1=420 mm; W1=697 mm; W1/2=348.5 mm; W_half=420 mm; bottom_rib=365 mm; bypass_sweep_dis=557.6 mm; wedge_dim1=247.5 mm
- 54-0600-33-1102100: ACtuator_T=25.92 mm; ADN=600 mm; Actuator_FLR=105 mm; BP_centre=88 mm; Body_H=589 mm; Body_L=667.2 mm; Body_T=292.5 mm; Body_W=250.5 mm; Body_rib_T=14.4 mm  [stored 0.0472441 ft]; Bonnet_FL_L=834 mm; Bonnet_FL_T=68.4 mm; Bonnet_FL_W=334 mm; Bonnet_dim1=133.44 mm; Bonnet_dim2=87.68 mm; Bonnet_dim3=977.74 mm; Bonnet_fillet=27.83 mm; Bore=300.06 mm; By_Vale_StemH1=270 mm; By_Vale_StemH2=283.5 mm; By_Vale_StemR1=18.56 mm; By_Vale_StemR2=33.4 mm; Bypass_DN=80 mm; Bypass_dim1=176 mm; Bypass_dim2=17.6 mm; Bypass_dim3=75.68 mm; Bypass_dis=592.45 mm; Bypass_dis/2=296.23 mm; Bypass_valve_H1=144 mm; Bypass_valve_H2=96 mm; Bypass_valve_H3=360 mm; Bypass_valve_W1=655.18 mm; Bypass_valve_W2=83.5 mm; Cut_dis=34.2 mm; DN=600.11 mm; FL_T=36 mm; Fillet=83.5 mm; H1=1178 mm; H2=440 mm; L=508 mm; OD=880 mm; PN=16 mm  [stored 0.0524934 ft]; Raised_dia=720 mm; Raised_dis=5 mm  [stored 0.0164042 ft]; Rib_H=471.2 mm; Rib_L=375.3 mm; Rib_W=150.3 mm; W=1117 mm; W-W1=420 mm; W1=697 mm; W1/2=348.5 mm; W_half=420 mm; bottom_rib=440 mm; bypass_sweep_dis=557.6 mm; wedge_dim1=275.55 mm
- 54-0600-34-0101100: ACtuator_T=21.6 mm  [stored 0.0708661 ft]; ADN=600 mm; Actuator_FLR=87.5 mm; BP_centre=78 mm; Body_H=589 mm; Body_L=667.2 mm; Body_T=292.5 mm; Body_W=250.5 mm; Body_rib_T=12 mm  [stored 0.0393701 ft]; Bonnet_FL_L=834 mm; Bonnet_FL_T=57 mm; Bonnet_FL_W=334 mm; Bonnet_dim1=133.44 mm; Bonnet_dim2=87.68 mm; Bonnet_dim3=977.74 mm; Bonnet_fillet=27.83 mm; Bore=300.06 mm; By_Vale_StemH1=270 mm; By_Vale_StemH2=283.5 mm; By_Vale_StemR1=18.56 mm; By_Vale_StemR2=33.4 mm; Bypass_DN=80 mm; Bypass_dim1=156 mm; Bypass_dim2=15.6 mm  [stored 0.0511811 ft]; Bypass_dim3=67.08 mm; Bypass_dis=592.45 mm; Bypass_dis/2=296.23 mm; Bypass_valve_H1=144 mm; Bypass_valve_H2=96 mm; Bypass_valve_H3=360 mm; Bypass_valve_W1=655.18 mm; Bypass_valve_W2=83.5 mm; Cut_dis=28.5 mm; DN=600.12 mm; FL_T=30 mm; Fillet=83.5 mm; H1=1178 mm; H2=440 mm; L=508 mm; OD=780 mm; PN=10 mm  [stored 0.0328084 ft]; Raised_dia=682 mm; Raised_dis=5 mm  [stored 0.0164042 ft]; Rib_H=471.2 mm; Rib_L=375.3 mm; Rib_W=150.3 mm; W=1117 mm; W-W1=420 mm; W1=697 mm; W1/2=348.5 mm; W_half=420 mm; bottom_rib=390 mm; bypass_sweep_dis=557.6 mm; wedge_dim1=275.55 mm
- 54-0600-34-1101100: ACtuator_T=25.92 mm; ADN=600 mm; Actuator_FLR=87.5 mm; BP_centre=88 mm; Body_H=589 mm; Body_L=667.2 mm; Body_T=292.5 mm; Body_W=250.5 mm; Body_rib_T=14.4 mm  [stored 0.0472441 ft]; Bonnet_FL_L=834 mm; Bonnet_FL_T=68.4 mm; Bonnet_FL_W=334 mm; Bonnet_dim1=133.44 mm; Bonnet_dim2=87.68 mm; Bonnet_dim3=977.74 mm; Bonnet_fillet=27.83 mm; Bore=300.07 mm; By_Vale_StemH1=270 mm; By_Vale_StemH2=283.5 mm; By_Vale_StemR1=18.56 mm; By_Vale_StemR2=33.4 mm; Bypass_DN=80 mm; Bypass_dim1=176 mm; Bypass_dim2=17.6 mm; Bypass_dim3=75.68 mm; Bypass_dis=592.45 mm; Bypass_dis/2=296.23 mm; Bypass_valve_H1=144 mm; Bypass_valve_H2=96 mm; Bypass_valve_H3=360 mm; Bypass_valve_W1=655.18 mm; Bypass_valve_W2=83.5 mm; Cut_dis=34.2 mm; DN=600.13 mm; FL_T=36 mm; Fillet=83.5 mm; H1=1178 mm; H2=440 mm; L=508 mm; OD=880 mm; PN=16 mm  [stored 0.0524934 ft]; Raised_dia=720 mm; Raised_dis=5 mm  [stored 0.0164042 ft]; Rib_H=471.2 mm; Rib_L=375.3 mm; Rib_W=150.3 mm; W=1117 mm; W-W1=420 mm; W1=697 mm; W1/2=348.5 mm; W_half=420 mm; bottom_rib=440 mm; bypass_sweep_dis=557.6 mm; wedge_dim1=275.55 mm

note: [stored X ft] marks values corroborated as IEEE doubles in the binary element streams (Revit-internal decimal feet)

## geometry (parser evidence)
native form markers: Sweep x13
no freeform markers — native parametric forms only
